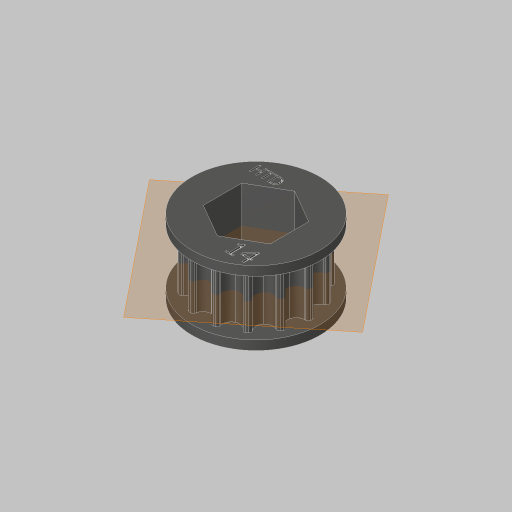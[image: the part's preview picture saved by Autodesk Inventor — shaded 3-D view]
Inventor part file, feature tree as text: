
AUTODESK INVENTOR PART (.ipt)
format: ipt  version: 2023.5 (Build 275446000, 446)  size: 1,080,320 bytes
history: native  units: in
note: dims shown in document units (in); Inventor stores cm internally (conversion verified against a paired STEP export)
features: sketch x5, extrude x4, projected_geometry x2, thicken_offset x1, plane x1, mirror x1, emboss x1, other x1
ambient origin geometry x8: Origin, YZ Plane, XZ Plane, XY Plane, X Axis, Y Axis, Z Axis, Center Point
bodies: Solid1 (feature_tree)
feature tree (16):
  extrude  "spline"  Depth=0.0394in
  thicken_offset  "Thicken1"
  plane  "Work Plane2"
  extrude  "side 1"  Depth=0.0394in
  mirror  "side 2"
  extrude  "spline tol"  Depth=0.0689in
  emboss  "Emboss1"
  extrude  "hex"  TaperAngle=0.0deg  [1 undecoded]
  sketch  "Sketch1"  dims[d0=0.3937in d1=0.0in d3=0.0394in]
  sketch  "Sketch2"  dims[d4=0.0394in d5=0.0625in]
  sketch  "Sketch3"  dims[d6=0.0689in d7=0.0in d8=0.003in]
  sketch  "Sketch4"  dims[d9=0.2339in d10=0.0in d11=0.0in]
  sketch  "Sketch5"  dims[d12=0.0125in d13=0.0in d14=0.502in d15=0.0in d16=0.0in]
  other  "14t HTD Pulley 9.53mm Wide"
  projected_geometry  "Project Cut Edges1"
  projected_geometry  "Project Cut Edges2"
note: 1 required parameter value undecoded (feature->parameter linkage not recoverable at this tier; creation-order binding heuristic only, values carry confidence <= 0.55)
